# Revit family: IVLB_MANUFACTURER_LF_FAMILYNAME
name_source: partatom
category: Lighting Fixtures
units: mm (PartAtom-declared; Revit-internal decimal feet)

## family parameters
Always vertical = Yes
Cut with Voids When Loaded = No
Light Source = Yes
OmniClass Number = 23.80.70.11.14
OmniClass Title = General Luminaries, Directional
Part Type = Normal
Room Calculation Point = Yes
Round Connector Dimension = Use Diameter
Shared = No
Work Plane-Based = No

## types (1)
- IVLB_MANUFACTURER_LF_FAMILYNAME
    Apparent Load = 19 VA
    Assembly Code = 63.0
    Calc_Symbol_L1 = 3 mm  [stored 0.00984252 ft]
    Calc_Symbol_L2 = 0 mm  [stored 0 ft]
    Color Filter = 16777215
    Dimming Lamp Color Temperature Shift = <None>
    ETIM Code = ETIMCODE
    Emit Shape Visible in Rendering = No
    Emit from Rectangle Length = 300 mm
    Emit from Rectangle Width = 300 mm
    GTIN Code = GTINCODE
    Housing_Material = Laminate, White
    IK Value = IKVALUE
    IP Value = IPVALUE
    ISBN Code = ISBNCODE
    IfcExportAs = IfcLightFixtureType
    IfcExportType = USERDEFINED
    L1 = 300 mm
    L2 = 300 mm
    L3 = 40 mm  [stored 0.131234 ft]
    Lamp = LED
    Luminous Flux (lm) = 500 lm
    Manufacturer = MANUFACTURER
    Model = FAMILYNAME
    Photometric Web File = _RC402BLED36S840OCSRDW62L62.IES
    Tilt Angle = 90.00°
    Type Comments = TYPENAME
    URL = https://www.ivlibrary.com
    Voltage = 230 V
    Wattage Comments = 19W

note: [stored X ft] marks values corroborated as IEEE doubles in the binary element streams (Revit-internal decimal feet)

## geometry (parser evidence)
native form markers: Sweep x2
no freeform markers — native parametric forms only
